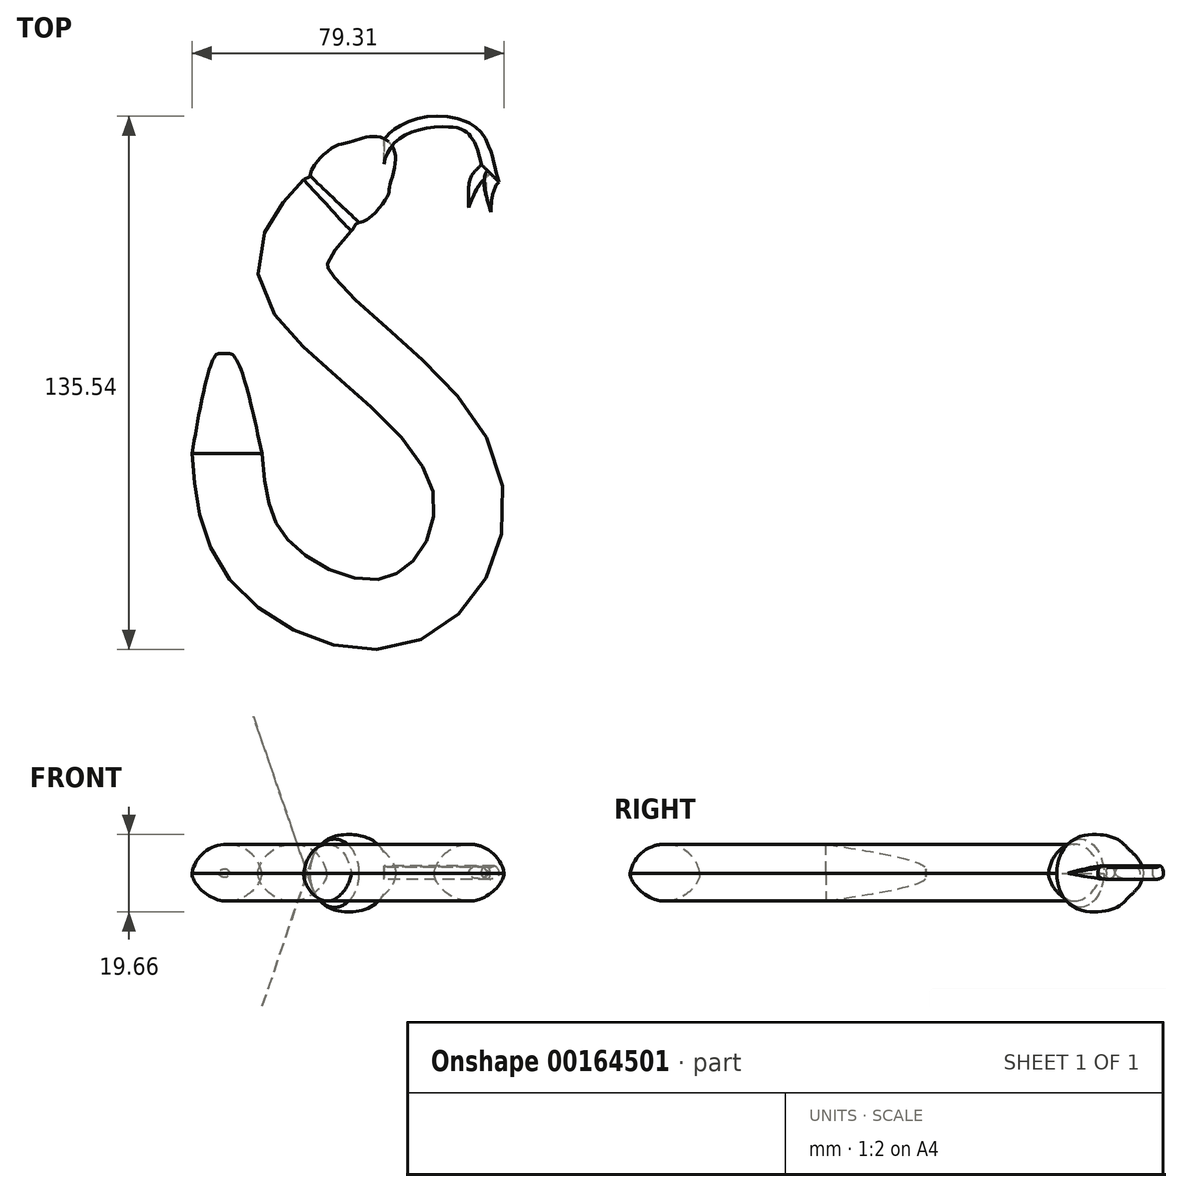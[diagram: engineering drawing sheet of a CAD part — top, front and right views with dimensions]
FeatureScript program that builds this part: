
annotation { "Feature Type Name" : "Feature", "Feature Type Description" : "" }
export const myFeature = defineFeature(function(context is Context, id is Id, definition is map)
    precondition{}
    {
        {
            var Q0;
            Q0=qCreatedBy(makeId("Top.planeOp"),FACE);
            var sketch = newSketch(context, id + "F0", { "sketchPlane" : qUnion([Q0])});
            skFitSpline(sketch, "E0", {"points": [v(0, 0) * mm, v(8.51, -27.68) * mm, v(45.25, -40.08) * mm, v(60.81, -3.56) * mm, v(18.54, 43.97) * mm, v(26.4, 62.65) * mm], "startDerivative": vector(13.43, -165.9) * mm, "endDerivative": vector(114.54, 124.21) * mm});
            skSolve(sketch);
        }
        {
            var Q0;
            Q0=qCreatedBy(makeId("Front.planeOp"),FACE);
            var sketch = newSketch(context, id + "F1", { "sketchPlane" : qUnion([Q0])});
            skArc(sketch, "E1", {"start": v(9.43, 0) * mm, "mid": v(0.53, 7.36) * mm, "end": v(-8.38, 0) * mm});
            skFitSpline(sketch, "E2", {"points": [v(-8.38, 0) * mm, v(0, -7.08) * mm, v(9.43, 0) * mm], "startDerivative": vector(0, -15.3) * mm, "endDerivative": vector(0, 20.44) * mm});
            skLineSegment(sketch, "E3", {"start": v(-8.38, -2.5) * mm, "end": v(-8.38, 0) * mm, "construction": true});
            skLineSegment(sketch, "E4", {"start": v(9.43, -3.47) * mm, "end": v(9.43, 0) * mm, "construction": true});
            skSolve(sketch);
        }
        {
            var Q0;
            Q0=makeQuery(id+"F1.imprint","IMPRINT",FACE,{"disambiguationData":[TD([[makeQuery(id+"F1.imprint","IMPRINT",EDGE,{"derivedFrom":sQuery(id+"F1.wireOp",EDGE,"E1")}),1.0]])]});
            var Q1;
            Q1=sQuery(id+"F0.wireOp",EDGE,"E0");
            sweep(context, id + "F2", {"profiles" : qUnion([Q0]), "path" : qUnion([Q1])});
        }
        {
            var Q0;
            Q0=makeQuery(id+"F1.imprint","IMPRINT",FACE,{"disambiguationData":[TD([[makeQuery(id+"F1.imprint","IMPRINT",EDGE,{"derivedFrom":sQuery(id+"F1.wireOp",EDGE,"E1")}),1.0]])]});
            var sketch = newSketch(context, id + "F3", { "sketchPlane" : qUnion([Q0])});
            skFitSpline(sketch, "E5", {"points": [v(0, -1) * mm, v(1.22, 0) * mm, v(0, 1.03) * mm, v(-1.61, 0) * mm, v(0, -1) * mm]});
            skSolve(sketch);
        }
        {
            var Q0;
            Q0 = qSketchRegion(id + "F3", true);
            extrude(context, id + "F4", {"entities" : qUnion([Q0]), "operationType" : NewBodyOperationType.ADD, "oppositeDirection" : true, "depth" : 25.4 * mm});
        }
        {
            var Q1;
            Q1=makeQuery(id+"F4.opExtrude","CAP_FACE",FACE,{"disambiguationData":[OSD([sQuery(id+"F3.wireOp",EDGE,"E5")])],"isStart":false});
            var Q2;
            Q2=makeQuery(id+"F1.imprint","IMPRINT",FACE,{"disambiguationData":[TD([[makeQuery(id+"F1.imprint","IMPRINT",EDGE,{"derivedFrom":sQuery(id+"F1.wireOp",EDGE,"E1")}),1.0]])]});
            loft(context, id + "F5", {"operationType" : NewBodyOperationType.ADD, "startCondition" : LoftEndDerivativeType.TANGENT_TO_PROFILE, "startMagnitude" : 1, "sheetProfilesArray" : [{ "sheetProfileEntities" : qUnion([Q1]) }, { "sheetProfileEntities" : qUnion([Q2]) }]});
        }
        {
            var Q0;
            Q0=qCreatedBy(makeId("Top.planeOp"),FACE);
            var sketch = newSketch(context, id + "F6", { "sketchPlane" : qUnion([Q0])});
            skPoint(sketch, "E6", {"position": v(34.14, 58.62) * mm});
            skPoint(sketch, "E7", {"position": v(21.02, 71.03) * mm});
            skFitSpline(sketch, "E8", {"points": [v(34.14, 58.62) * mm, v(41.2, 65.13) * mm, v(41.84, 67.66) * mm, v(43.34, 74.6) * mm, v(41.65, 79.08) * mm], "startDerivative": vector(23.29, 2.5) * mm, "endDerivative": vector(-15.75, 14.07) * mm});
            skLineSegment(sketch, "E9", {"start": v(27.5, 64.2) * mm, "end": v(42.74, 80.22) * mm});
            skLineSegment(sketch, "E10", {"start": v(34.14, 58.62) * mm, "end": v(27.87, 64.59) * mm});
            skSolve(sketch);
        }
        {
            var Q0;
            Q0=makeQuery(id+"F6.imprint","IMPRINT",FACE,{"disambiguationData":[TD([[makeQuery(id+"F6.imprint","IMPRINT",EDGE,{"derivedFrom":sQuery(id+"F6.wireOp",EDGE,"E8")}),1.0]])]});
            var Q1;
            Q1=sQuery(id+"F6.wireOp",EDGE,"E9");
            revolve(context, id + "F7", {"entities" : qUnion([Q0]), "axis" : qUnion([Q1]), "revolveType" : RevolveType.FULL});
        }
        {
            var Q0;
            Q0=qCreatedBy(makeId("Top.planeOp"),FACE);
            var sketch = newSketch(context, id + "F8", { "sketchPlane" : qUnion([Q0])});
            skFitSpline(sketch, "E11", {"points": [v(40.38, 77.9) * mm, v(61.53, 83.14) * mm, v(68.31, 70.29) * mm], "startDerivative": vector(23.6, 40.33) * mm, "endDerivative": vector(9.8, -36.29) * mm});
            skLineSegment(sketch, "E12", {"start": v(68.31, 70.29) * mm, "end": v(76.17, 70.29) * mm});
            skLineSegment(sketch, "E13", {"start": v(68.31, 70.29) * mm, "end": v(64.93, 65.57) * mm});
            skLineSegment(sketch, "E14", {"start": v(64.93, 65.57) * mm, "end": v(64.93, 75.5) * mm});
            skLineSegment(sketch, "E15", {"start": v(65.87, 78.3) * mm, "end": v(64.93, 75.5) * mm});
            skPoint(sketch, "E16", {"position": v(61.96, 62.47) * mm});
            skPoint(sketch, "E17", {"position": v(67.55, 61.4) * mm});
            skSolve(sketch);
        }
        {
            var Q0;
            Q0=qCreatedBy(makeId("Right.planeOp"),FACE);
            var Q1;
            Q1=sQuery(id+"F8.wireOp",VERTEX,"E11.0.internal");
            cPlane(context, id + "F9", {"entities" : qUnion([Q0, Q1]), "cplaneType" : CPlaneType.PLANE_POINT, "offset" : 25.4 * mm, "width" : 152.4 * mm, "height" : 152.4 * mm});
        }
        {
            var Q0;
            Q0=qCreatedBy(id+"F9.planeOp",FACE);
            var sketch = newSketch(context, id + "F10", { "sketchPlane" : qUnion([Q0])});
            skFitSpline(sketch, "E18", {"points": [v(73.72, -0.59) * mm, v(74.48, 1.6) * mm, v(76.36, 1.45) * mm, v(78.63, 1.71) * mm, v(79.5, -0.7) * mm, v(73.72, -0.59) * mm]});
            skSolve(sketch);
        }
        {
            var Q0;
            Q0 = qSketchRegion(id + "F10", true);
            var Q1;
            Q1=sQuery(id+"F10.wireOp",EDGE,"E18");
            var Q2;
            Q2=sQuery(id+"F8.wireOp",EDGE,"E11");
            sweep(context, id + "F11", {"profiles" : qUnion([Q0]), "surfaceProfiles" : qUnion([Q1]), "path" : qUnion([Q2])});
        }
        {
            var Q0;
            Q0=makeQuery(id+"F11.opSweep","CAP_FACE",FACE,{"disambiguationData":[OSD([sQuery(id+"F8.wireOp",VERTEX,"E11.end"),sQuery(id+"F10.wireOp",EDGE,"E18")])],"isStart":false});
            var sketch = newSketch(context, id + "F12", { "sketchPlane" : qUnion([Q0])});
            skLineSegment(sketch, "E19", {"start": v(-1.94, 1.47) * mm, "end": v(-1.94, -1.51) * mm});
            skSolve(sketch);
        }
        {
            var Q0;
            {var subQ0=sQuery(id+"F12.wireOp",EDGE,"E19");Q0=makeQuery(id+"F12.imprint","IMPRINT",FACE,{"disambiguationData":[TD([[makeQuery(id+"F12.imprint","IMPRINT",EDGE,{"derivedFrom":subQ0}),-1.0]])]});}
            extrude(context, id + "F13", {"entities" : qUnion([Q0]), "operationType" : NewBodyOperationType.ADD, "depth" : 2.54 * mm});
        }
        {
            var Q0;
            {var subQ0=sQuery(id+"F12.wireOp",EDGE,"E19");var subQ1=sQuery(id+"F10.wireOp",EDGE,"E18");var subQ2=sQuery(id+"F8.wireOp",VERTEX,"E11.end");Q0=makeQuery(id+"F13.opExtrude","SWEPT_EDGE",EDGE,{"disambiguationData":[OSD([subQ2,subQ1,subQ0]),TDD([makeQuery(id+"F12.imprint","INTERSECT",VERTEX,{"disambiguationData":[OD(0.0)],"derivedFrom":[makeQuery(id+"F11.opSweep","CAP_EDGE",EDGE,{"disambiguationData":[OSD([subQ2,subQ1])],"isStart":false}),subQ0]})])]});}
            fillet(context, id + "F14", {"entities" : qUnion([Q0]), "radius" : 1.27 * mm, "tangentPropagation" : true, "allowEdgeOverflow" : false});
        }
        {
            var Q0;
            {var subQ0=sQuery(id+"F12.wireOp",EDGE,"E19");var subQ1=sQuery(id+"F10.wireOp",EDGE,"E18");var subQ2=sQuery(id+"F8.wireOp",VERTEX,"E11.end");Q0=makeQuery(id+"F13.opExtrude","SWEPT_EDGE",EDGE,{"disambiguationData":[OSD([subQ2,subQ1,subQ0]),TDD([makeQuery(id+"F12.imprint","INTERSECT",VERTEX,{"disambiguationData":[OD(1.0)],"derivedFrom":[makeQuery(id+"F11.opSweep","CAP_EDGE",EDGE,{"disambiguationData":[OSD([subQ2,subQ1])],"isStart":false}),subQ0]})])]});}
            fillet(context, id + "F15", {"entities" : qUnion([Q0]), "radius" : 1.02 * mm, "tangentPropagation" : true, "allowEdgeOverflow" : false});
        }
        {
            var Q1;
            Q1=sQuery(id+"F8.wireOp",VERTEX,"E16");
            var Q2;
            Q2=makeQuery(id+"F13.opExtrude","CAP_FACE",FACE,{"disambiguationData":[OSD([sQuery(id+"F8.wireOp",VERTEX,"E11.end"),sQuery(id+"F10.wireOp",EDGE,"E18"),sQuery(id+"F12.wireOp",EDGE,"E19")])],"isStart":false});
            loft(context, id + "F16", {"operationType" : NewBodyOperationType.ADD, "endCondition" : LoftEndDerivativeType.NORMAL_TO_PROFILE, "endMagnitude" : 1, "sheetProfilesArray" : [{ "sheetProfileEntities" : qUnion([Q1]) }, { "sheetProfileEntities" : qUnion([Q2]) }]});
        }
        {
            var Q1;
            Q1=makeQuery(id+"F11.opSweep","CAP_FACE",FACE,{"disambiguationData":[OSD([sQuery(id+"F8.wireOp",VERTEX,"E11.end"),sQuery(id+"F10.wireOp",EDGE,"E18")])],"isStart":false});
            var Q2;
            Q2=sQuery(id+"F8.wireOp",VERTEX,"E17");
            loft(context, id + "F17", {"operationType" : NewBodyOperationType.ADD, "startCondition" : LoftEndDerivativeType.NORMAL_TO_PROFILE, "startMagnitude" : 1, "sheetProfilesArray" : [{ "sheetProfileEntities" : qUnion([Q1]) }, { "sheetProfileEntities" : qUnion([Q2]) }]});
        }
        {
            var Q1;
            Q1=makeQuery(id+"F2.opSweep","CAP_FACE",FACE,{"disambiguationData":[OSD([sQuery(id+"F0.wireOp",VERTEX,"E0.end"),sQuery(id+"F1.wireOp",EDGE,"E1"),sQuery(id+"F1.wireOp",EDGE,"E2")])],"isStart":false});
            var Q2;
            Q2=makeQuery(id+"F7.opRevolve","SWEPT_FACE",FACE,{"disambiguationData":[OSD([sQuery(id+"F6.wireOp",EDGE,"E10")])]});
            loft(context, id + "F18", {"startCondition" : LoftEndDerivativeType.NORMAL_TO_PROFILE, "startMagnitude" : 1, "endCondition" : LoftEndDerivativeType.MATCH_CURVATURE, "endMagnitude" : 1, "sheetProfilesArray" : [{ "sheetProfileEntities" : qUnion([Q1]) }, { "sheetProfileEntities" : qUnion([Q2]) }]});
        }
    });
